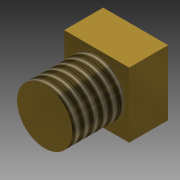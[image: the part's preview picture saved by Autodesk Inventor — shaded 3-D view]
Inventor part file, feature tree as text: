
AUTODESK INVENTOR PART (.ipt)
format: ipt  version: 2011 (Build 150239000, 239)  size: 90,624 bytes
history: native  units: in
note: dims shown in document units (in); Inventor stores cm internally (conversion verified against a paired STEP export)
features: extrude x2, sketch x2, thread x1
ambient origin geometry x8: Origin, YZ Plane, XZ Plane, XY Plane, X Axis, Y Axis, Z Axis, Center Point
bodies: Solid1 (feature_tree)
feature tree (5):
  extrude  "Extrusion1"  Depth=0.5in
  extrude  "Extrusion2"  Depth=0.425in
  thread  "Thread1"  [1 undecoded]
  sketch  "Sketch1"  dims[d0=0.5in d1=0.5in]
  sketch  "Sketch2"  dims[d2=0.3in d3=0.0in d4=0.425in d5=0.4in d6=0.0in d7=1.0in d8=0.0in]
note: 1 required parameter value undecoded (feature->parameter linkage not recoverable at this tier; creation-order binding heuristic only, values carry confidence <= 0.55)
